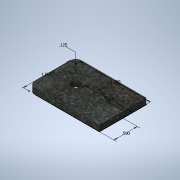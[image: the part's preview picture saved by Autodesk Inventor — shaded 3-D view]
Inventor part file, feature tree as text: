
AUTODESK INVENTOR PART (.ipt)
format: ipt  version: 2021 (Build 250183000, 183)  size: 118,272 bytes
history: native  units: in
note: dims shown in document units (in); Inventor stores cm internally (conversion verified against a paired STEP export)
features: sketch x1, extrude x1, hole x1
ambient origin geometry x8: Origin, YZ Plane, XZ Plane, XY Plane, X Axis, Y Axis, Z Axis, Center Point
bodies: Solid1 (feature_tree)
feature tree (3):
  sketch  "Sketch1"  dims[d0=1.5in d1=1.0in d2=0.5in d3=1.0in d5=0.125in d6=0.0in d7=0.125in d8=0.201in d9=0.75in d10=0.385in d11=0.25in d12=0.5635in d13=1.0in d14=0.8108in]
  extrude  "Extrusion1"  Depth=1.0in
  hole  "Hole1"  [1 undecoded]
note: 1 required parameter value undecoded (feature->parameter linkage not recoverable at this tier; creation-order binding heuristic only, values carry confidence <= 0.55)
